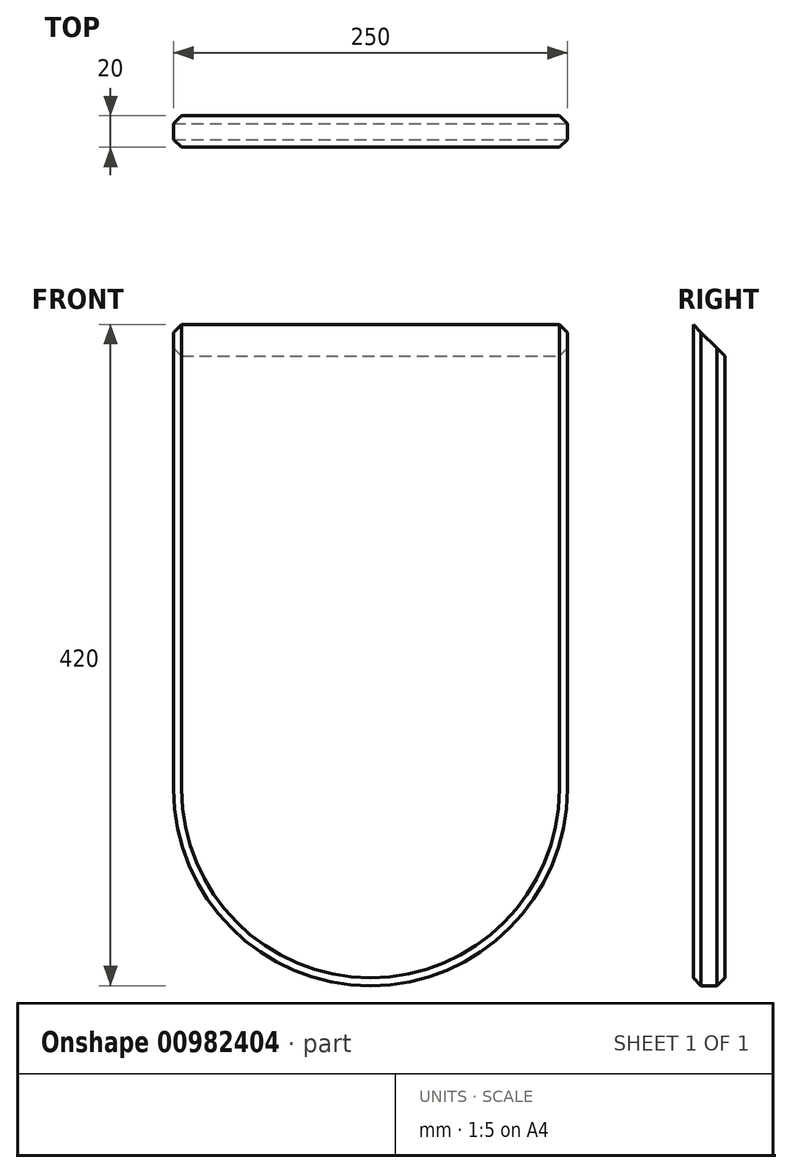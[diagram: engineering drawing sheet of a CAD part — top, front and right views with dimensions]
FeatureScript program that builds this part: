
annotation { "Feature Type Name" : "Feature", "Feature Type Description" : "" }
export const myFeature = defineFeature(function(context is Context, id is Id, definition is map)
    precondition{}
    {
        {
            var Q0;
            Q0=qCreatedBy(makeId("Front.planeOp"),FACE);
            var sketch = newSketch(context, id + "F0", { "sketchPlane" : qUnion([Q0])});
            skArc(sketch, "E0", {"start": v(-78.42, -102.16) * mm, "mid": v(46.58, -227.16) * mm, "end": v(171.58, -102.16) * mm});
            skLineSegment(sketch, "E1", {"start": v(-78.42, -102.16) * mm, "end": v(-78.42, 192.84) * mm});
            skLineSegment(sketch, "E2", {"start": v(-78.42, 192.84) * mm, "end": v(171.58, 192.84) * mm});
            skLineSegment(sketch, "E3", {"start": v(171.58, 192.84) * mm, "end": v(171.58, -102.16) * mm});
            skLineSegment(sketch, "E4", {"start": v(46.58, -227.16) * mm, "end": v(203.02, -227.16) * mm});
            skSolve(sketch);
        }
        {
            var Q0;
            Q0=makeQuery(id+"F0.imprint","IMPRINT",FACE,{"disambiguationData":[TD([[makeQuery(id+"F0.imprint","IMPRINT",EDGE,{"derivedFrom":sQuery(id+"F0.wireOp",EDGE,"E0")}),1.0]])]});
            extrude(context, id + "F1", {"entities" : qUnion([Q0]), "depth" : 20 * mm, "offsetDistance" : 25 * mm});
        }
        {
            var Q0;
            Q0=makeQuery(id+"F1.opExtrude","CAP_EDGE",EDGE,{"disambiguationData":[OSD([sQuery(id+"F0.wireOp",EDGE,"E1")])],"isStart":true});
            var Q1;
            Q1=makeQuery(id+"F1.opExtrude","CAP_EDGE",EDGE,{"disambiguationData":[OSD([sQuery(id+"F0.wireOp",EDGE,"E1")])],"isStart":false});
            chamfer(context, id + "F2", {"entities" : qUnion([Q0, Q1]), "width" : 5 * mm, "tangentPropagation" : true});
        }
        {
            var Q0;
            Q0=makeQuery(id+"F1.opExtrude","CAP_EDGE",EDGE,{"disambiguationData":[OSD([sQuery(id+"F0.wireOp",EDGE,"E2")])],"isStart":true});
            chamfer(context, id + "F3", {"entities" : qUnion([Q0]), "width" : 20 * mm, "tangentPropagation" : true});
        }
    });
